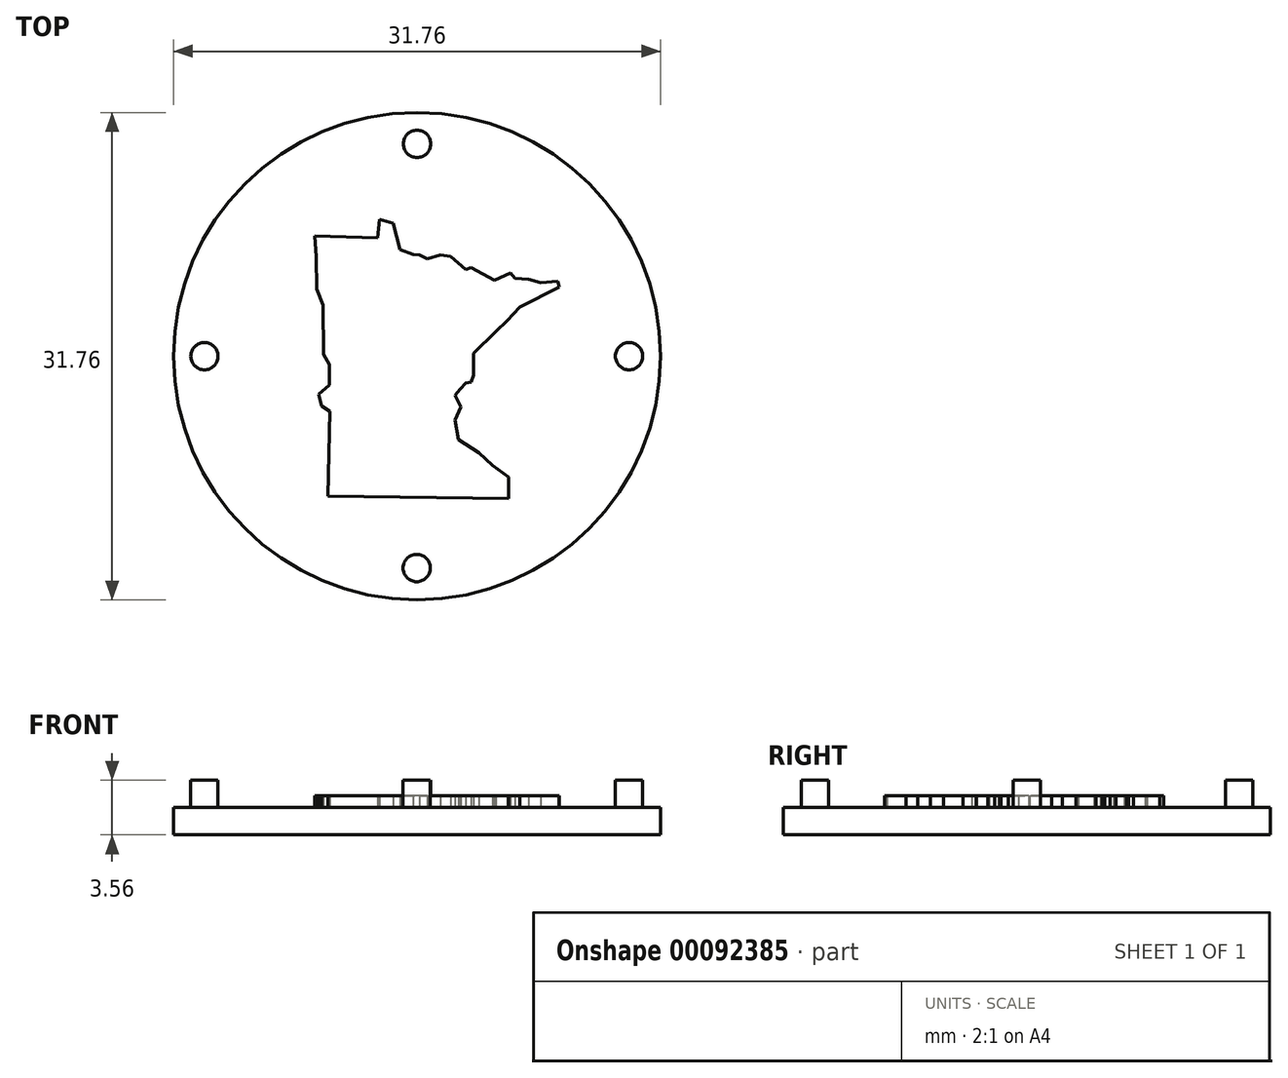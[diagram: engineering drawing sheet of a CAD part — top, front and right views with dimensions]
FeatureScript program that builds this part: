
annotation { "Feature Type Name" : "Feature", "Feature Type Description" : "" }
export const myFeature = defineFeature(function(context is Context, id is Id, definition is map)
    precondition{}
    {
        {
            var Q0;
            Q0=qCreatedBy(makeId("Top.planeOp"),FACE);
            var sketch = newSketch(context, id + "F0", { "sketchPlane" : qUnion([Q0])});
            skCircle(sketch, "E0", {"center": v(0, 0) * mm, "radius": 15.88 * mm});
            skSolve(sketch);
        }
        {
            var Q0;
            Q0=qSketchRegion(id+"F0",true);
            extrude(context, id + "F1", {"entities" : qUnion([Q0]), "oppositeDirection" : true, "depth" : 1.78 * mm});
        }
        {
            var Q0;
            Q0=makeQuery(id+"F1.opExtrude","CAP_FACE",FACE,{"disambiguationData":[OSD([sQuery(id+"F0.wireOp",EDGE,"E0")])],"isStart":true});
            var sketch = newSketch(context, id + "F2", { "sketchPlane" : qUnion([Q0])});
            skCircle(sketch, "E1", {"center": v(0, 0) * mm, "radius": 12.7 * mm});
            skSolve(sketch);
        }
        {
            var Q0;
            Q0=makeQuery(id+"F2.imprint","IMPRINT",FACE,{"disambiguationData":[TD([[makeQuery(id+"F2.imprint","IMPRINT",EDGE,{"derivedFrom":sQuery(id+"F2.wireOp",EDGE,"E1")}),-1.0]])]});
            var sketch = newSketch(context, id + "F3", { "sketchPlane" : qUnion([Q0])});
            skCircle(sketch, "E2", {"center": v(0, 13.84) * mm, "radius": 0.89 * mm});
            skCircle(sketch, "E3", {"center": v(-13.86, 0) * mm, "radius": 0.89 * mm});
            skCircle(sketch, "E4", {"center": v(-0.03, -13.8) * mm, "radius": 0.89 * mm});
            skCircle(sketch, "E5", {"center": v(13.82, 0) * mm, "radius": 0.89 * mm});
            skSolve(sketch);
        }
        {
            var Q0;
            Q0=qSketchRegion(id+"F3",true);
            extrude(context, id + "F4", {"entities" : qUnion([Q0]), "operationType" : NewBodyOperationType.ADD, "depth" : 1.78 * mm});
        }
        {
            var Q0;
            Q0=makeQuery(id+"F2.imprint","IMPRINT",FACE,{"disambiguationData":[TD([[makeQuery(id+"F2.imprint","IMPRINT",EDGE,{"derivedFrom":sQuery(id+"F2.wireOp",EDGE,"E1")}),1.0]])]});
            var sketch = newSketch(context, id + "F5", { "sketchPlane" : qUnion([Q0])});
            skLineSegment(sketch, "E6", {"start": v(-2.56, 7.7) * mm, "end": v(-6.67, 7.84) * mm});
            skLineSegment(sketch, "E7", {"start": v(-6.67, 7.84) * mm, "end": v(-6.56, 6.46) * mm});
            skLineSegment(sketch, "E8", {"start": v(-6.56, 6.46) * mm, "end": v(-6.53, 4.37) * mm});
            skLineSegment(sketch, "E9", {"start": v(-6.53, 4.37) * mm, "end": v(-6.14, 3.34) * mm});
            skLineSegment(sketch, "E10", {"start": v(-6.14, 3.34) * mm, "end": v(-6.1, 0.11) * mm});
            skLineSegment(sketch, "E11", {"start": v(-6.1, 0.11) * mm, "end": v(-5.71, -0.56) * mm});
            skLineSegment(sketch, "E12", {"start": v(-5.71, -0.56) * mm, "end": v(-5.71, -1.87) * mm});
            skLineSegment(sketch, "E13", {"start": v(-5.71, -1.87) * mm, "end": v(-6.42, -2.47) * mm});
            skLineSegment(sketch, "E14", {"start": v(-6.42, -2.47) * mm, "end": v(-6.2, -3.25) * mm});
            skLineSegment(sketch, "E15", {"start": v(-6.2, -3.25) * mm, "end": v(-5.68, -3.6) * mm});
            skLineSegment(sketch, "E16", {"start": v(-5.68, -3.6) * mm, "end": v(-5.82, -9.13) * mm});
            skLineSegment(sketch, "E17", {"start": v(-5.82, -9.13) * mm, "end": v(5.98, -9.27) * mm});
            skLineSegment(sketch, "E18", {"start": v(5.98, -9.27) * mm, "end": v(5.98, -7.9) * mm});
            skLineSegment(sketch, "E19", {"start": v(5.98, -7.9) * mm, "end": v(4.92, -7.11) * mm});
            skLineSegment(sketch, "E20", {"start": v(4.92, -7.11) * mm, "end": v(4.03, -6.3) * mm});
            skLineSegment(sketch, "E21", {"start": v(4.03, -6.3) * mm, "end": v(2.68, -5.45) * mm});
            skLineSegment(sketch, "E22", {"start": v(2.68, -5.45) * mm, "end": v(2.47, -4.17) * mm});
            skLineSegment(sketch, "E23", {"start": v(2.47, -4.17) * mm, "end": v(2.86, -3.32) * mm});
            skLineSegment(sketch, "E24", {"start": v(2.86, -3.32) * mm, "end": v(2.47, -2.54) * mm});
            skLineSegment(sketch, "E25", {"start": v(2.47, -2.54) * mm, "end": v(2.83, -2.12) * mm});
            skLineSegment(sketch, "E26", {"start": v(2.83, -2.12) * mm, "end": v(3.18, -1.76) * mm});
            skLineSegment(sketch, "E27", {"start": v(3.18, -1.76) * mm, "end": v(3.53, -1.7) * mm});
            skLineSegment(sketch, "E28", {"start": v(3.53, -1.7) * mm, "end": v(3.68, -1.23) * mm});
            skLineSegment(sketch, "E29", {"start": v(3.68, -1.23) * mm, "end": v(3.68, 0.18) * mm});
            skLineSegment(sketch, "E30", {"start": v(3.68, 0.18) * mm, "end": v(5.13, 1.6) * mm});
            skLineSegment(sketch, "E31", {"start": v(5.13, 1.6) * mm, "end": v(5.87, 2.31) * mm});
            skLineSegment(sketch, "E32", {"start": v(5.87, 2.31) * mm, "end": v(6.69, 3.2) * mm});
            skLineSegment(sketch, "E33", {"start": v(6.69, 3.2) * mm, "end": v(9.27, 4.5) * mm});
            skLineSegment(sketch, "E34", {"start": v(9.27, 4.5) * mm, "end": v(9.17, 4.9) * mm});
            skLineSegment(sketch, "E35", {"start": v(9.17, 4.9) * mm, "end": v(8.07, 4.8) * mm});
            skLineSegment(sketch, "E36", {"start": v(8.07, 4.8) * mm, "end": v(7.25, 5) * mm});
            skLineSegment(sketch, "E37", {"start": v(7.25, 5) * mm, "end": v(6.37, 5.07) * mm});
            skLineSegment(sketch, "E38", {"start": v(6.37, 5.07) * mm, "end": v(6.08, 5.43) * mm});
            skLineSegment(sketch, "E39", {"start": v(6.08, 5.43) * mm, "end": v(5.06, 4.93) * mm});
            skLineSegment(sketch, "E40", {"start": v(5.06, 4.93) * mm, "end": v(3.53, 5.78) * mm});
            skLineSegment(sketch, "E41", {"start": v(3.53, 5.78) * mm, "end": v(3.18, 5.64) * mm});
            skLineSegment(sketch, "E42", {"start": v(3.18, 5.64) * mm, "end": v(2.19, 6.5) * mm});
            skLineSegment(sketch, "E43", {"start": v(2.19, 6.5) * mm, "end": v(1.51, 6.6) * mm});
            skLineSegment(sketch, "E44", {"start": v(1.51, 6.6) * mm, "end": v(0.66, 6.35) * mm});
            skLineSegment(sketch, "E45", {"start": v(0.66, 6.35) * mm, "end": v(0.17, 6.6) * mm});
            skLineSegment(sketch, "E46", {"start": v(0.17, 6.6) * mm, "end": v(-0.26, 6.63) * mm});
            skLineSegment(sketch, "E47", {"start": v(-0.26, 6.63) * mm, "end": v(-1.1, 6.95) * mm});
            skLineSegment(sketch, "E48", {"start": v(-1.1, 6.95) * mm, "end": v(-1.57, 8.65) * mm});
            skLineSegment(sketch, "E49", {"start": v(-1.57, 8.65) * mm, "end": v(-2.45, 8.9) * mm});
            skLineSegment(sketch, "E50", {"start": v(-2.45, 8.9) * mm, "end": v(-2.56, 7.7) * mm});
            skSolve(sketch);
        }
        {
            var Q0;
            Q0 = qSketchRegion(id + "F5", true);
            extrude(context, id + "F6", {"entities" : qUnion([Q0]), "operationType" : NewBodyOperationType.ADD, "depth" : 0.76 * mm});
        }
    });
